# Revit family: Plumbing_Valves_Bermad_430_Pressure_Sustaining_Valve Threaded 1.5in-3in
name_source: partatom
category: Pipe Accessories
units: mm (PartAtom-declared; Revit-internal decimal feet)

## family parameters
Always vertical = No
Cut with Voids When Loaded = No
Part Type = Valve - Breaks Into
Round Connector Dimension = Use Diameter
Shared = No
Work Plane-Based = No

## types (4) — shared parameters
Assembly Code = D2020300
Body_Type = Threaded
CPort_Dim = 40 mm  [stored 0.131234 ft]
D_Table = 400 Revit Sizes
Description = Pressure Relief / Sustaining Valve
Flanged_Body = No
Grooved_Body = No
M = 160 mm
Manufacturer = Bermad
Max Working Water Pressure = 16.0 bar
Max Working Water Temperature = 50 °C
Model = 430
Port_Dim = 30 mm  [stored 0.0984252 ft]
Product url = www.bermad.com/product/bc-430-p/
T_from_port = 220 mm
Threaded_Body = Yes
URL = www.Bermad.com

## per-type parameters (varying)
- 1.5" - DN40: Body_Dim=57 mm  [stored 0.187008 ft]; CChamper_Rad=11 mm  [stored 0.0360892 ft]; Cover_Dim=118 mm; Flange_Dim=54 mm  [stored 0.177165 ft]; Flange_Thick=24 mm  [stored 0.0787402 ft]; H=95 mm; H1=17 mm  [stored 0.0557743 ft]; H2=12 mm  [stored 0.0393701 ft]; H2_Plus_H3=27 mm  [stored 0.0885827 ft]; H3=15 mm  [stored 0.0492126 ft]; H4=16 mm  [stored 0.0524934 ft]; H5=6 mm  [stored 0.019685 ft]; H5_Plus_H6=7 mm; H6=1 mm  [stored 0.00328084 ft]; H_Plus_M=255 mm; K Coefficient=30; L=150 mm; Nominal_Diameter=40 mm  [stored 0.131234 ft]; Port_Down_X=44 mm; Port_Down_Y=6 mm  [stored 0.019685 ft]; Port_Up_X=44 mm; Port_Up_Y=5 mm  [stored 0.0164042 ft]; Port_W=37 mm; Port_h=29 mm  [stored 0.0951444 ft]; Port_h_Dim=40 mm  [stored 0.131234 ft]; Port_h_X=32 mm  [stored 0.104987 ft]; W=118 mm; Weight=2.00 kgf; h=29 mm  [stored 0.0951444 ft]
- 2" - DN50: Body_Dim=75 mm; CChamper_Rad=11 mm  [stored 0.0360892 ft]; Cover_Dim=118 mm; Flange_Dim=72 mm; Flange_Thick=27 mm  [stored 0.0885827 ft]; H=116 mm; H1=29 mm  [stored 0.0951444 ft]; H2=11 mm  [stored 0.0360892 ft]; H2_Plus_H3=25 mm  [stored 0.082021 ft]; H3=14 mm  [stored 0.0459318 ft]; H4=17 mm  [stored 0.0557743 ft]; H5=4 mm  [stored 0.0131234 ft]; H5_Plus_H6=5 mm  [stored 0.0164042 ft]; H6=1 mm  [stored 0.00328084 ft]; H_Plus_M=276 mm; K Coefficient=57; L=180 mm; Nominal_Diameter=50 mm  [stored 0.164042 ft]; Port_Down_X=53 mm  [stored 0.173885 ft]; Port_Down_Y=6 mm  [stored 0.019685 ft]; Port_Up_X=53 mm  [stored 0.173885 ft]; Port_Up_Y=5 mm  [stored 0.0164042 ft]; Port_W=51 mm  [stored 0.167323 ft]; Port_h=35 mm  [stored 0.114829 ft]; Port_h_Dim=40 mm  [stored 0.131234 ft]; Port_h_X=32 mm  [stored 0.104987 ft]; W=118 mm; Weight=4.00 kgf; h=36 mm  [stored 0.11811 ft]
- 2.5" - DN65: Body_Dim=95 mm; CChamper_Rad=18 mm  [stored 0.0590551 ft]; Cover_Dim=132 mm; Flange_Dim=90 mm; Flange_Thick=30 mm  [stored 0.0984252 ft]; H=135 mm; H1=32 mm  [stored 0.104987 ft]; H2=16 mm  [stored 0.0524934 ft]; H2_Plus_H3=36 mm  [stored 0.11811 ft]; H3=20 mm  [stored 0.0656168 ft]; H4=17 mm  [stored 0.0557743 ft]; H5=4 mm  [stored 0.0131234 ft]; H5_Plus_H6=5 mm  [stored 0.0164042 ft]; H6=1 mm  [stored 0.00328084 ft]; H_Plus_M=295 mm; K Coefficient=78; L=210 mm; Nominal_Diameter=65 mm; Port_Down_X=65 mm; Port_Down_Y=12 mm  [stored 0.0393701 ft]; Port_Up_X=60 mm; Port_Up_Y=10 mm  [stored 0.0328084 ft]; Port_W=49 mm  [stored 0.160761 ft]; Port_h=43 mm  [stored 0.141076 ft]; Port_h_Dim=60 mm; Port_h_X=20 mm  [stored 0.0656168 ft]; W=132 mm; Weight=5.70 kgf; h=45 mm  [stored 0.147638 ft]
- 3" - DN80: Body_Dim=112 mm; CChamper_Rad=11 mm  [stored 0.0360892 ft]; Cover_Dim=170 mm; Flange_Dim=108 mm; Flange_Thick=32 mm  [stored 0.104987 ft]; H=168 mm; H1=42 mm  [stored 0.137795 ft]; H2=23 mm; H2_Plus_H3=41 mm  [stored 0.134514 ft]; H3=18 mm  [stored 0.0590551 ft]; H4=22 mm  [stored 0.0721785 ft]; H5=9 mm  [stored 0.0295276 ft]; H5_Plus_H6=9 mm  [stored 0.0295276 ft]; H6=0 mm  [stored 0 ft]; H_Plus_M=328 mm; K Coefficient=136; L=255 mm; Nominal_Diameter=80 mm; Port_Down_X=78 mm; Port_Down_Y=18 mm  [stored 0.0590551 ft]; Port_Up_X=75 mm; Port_Up_Y=13 mm  [stored 0.0426509 ft]; Port_W=57 mm  [stored 0.187008 ft]; Port_h=10 mm  [stored 0.0328084 ft]; Port_h_Dim=10 mm  [stored 0.0328084 ft]; Port_h_X=75 mm; W=170 mm; Weight=13.00 kgf; h=54 mm  [stored 0.177165 ft]

note: [stored X ft] marks values corroborated as IEEE doubles in the binary element streams (Revit-internal decimal feet)

## geometry (parser evidence)
native form markers: Sweep x1
no freeform markers — native parametric forms only
